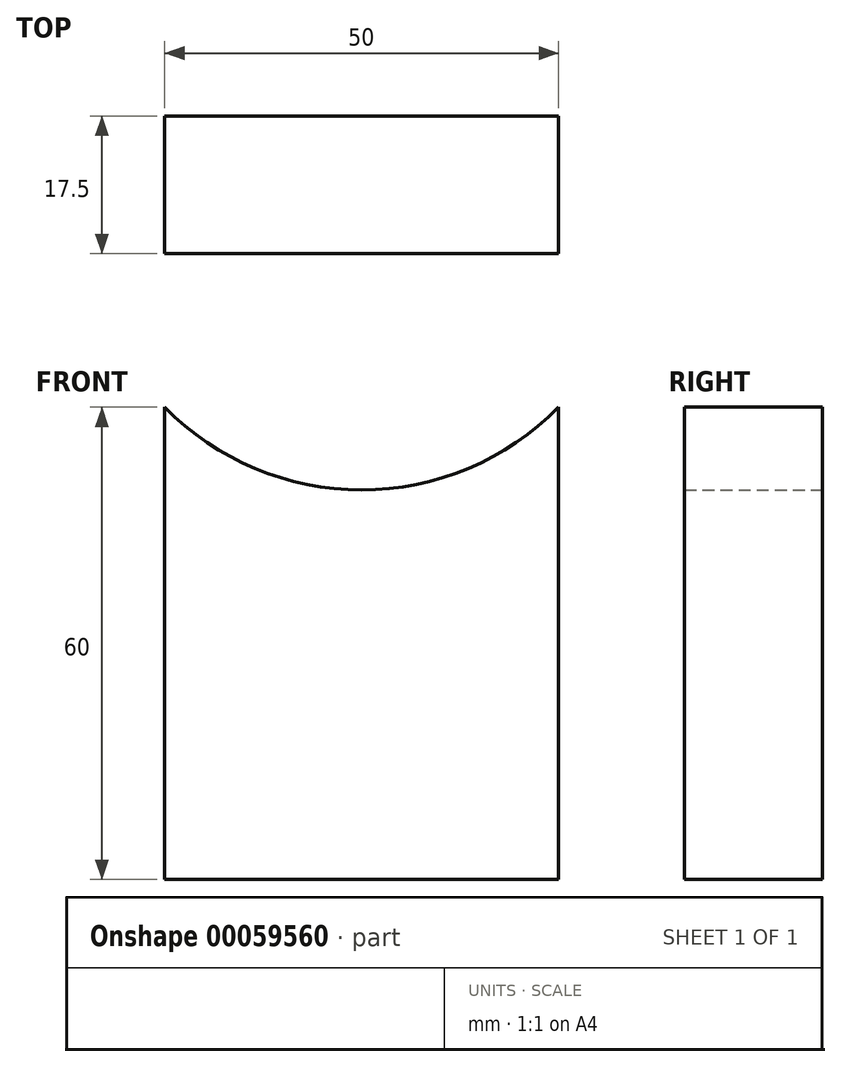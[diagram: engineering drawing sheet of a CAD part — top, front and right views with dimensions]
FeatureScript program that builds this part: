
annotation { "Feature Type Name" : "Feature", "Feature Type Description" : "" }
export const myFeature = defineFeature(function(context is Context, id is Id, definition is map)
    precondition{}
    {
        {
            var Q0;
            Q0=qCreatedBy(makeId("Front.planeOp"),FACE);
            var sketch = newSketch(context, id + "F0", { "sketchPlane" : qUnion([Q0])});
            skLineSegment(sketch, "E0.rect.top", {"start": v(-25, -30) * mm, "end": v(25, -30) * mm});
            skLineSegment(sketch, "E0.rect.left", {"start": v(-25, 30) * mm, "end": v(-25, -30) * mm});
            skLineSegment(sketch, "E0.rect.right", {"start": v(25, 30) * mm, "end": v(25, -30) * mm});
            skPoint(sketch, "E0.rect.middle", {"position": v(0, 0) * mm});
            skArc(sketch, "E1", {"start": v(-25, 30) * mm, "mid": v(0, 19.5) * mm, "end": v(25, 30) * mm});
            skSolve(sketch);
        }
        {
            var Q0;
            Q0=makeQuery(id+"F0.imprint","IMPRINT",FACE,{"disambiguationData":[TD([[makeQuery(id+"F0.imprint","IMPRINT",EDGE,{"derivedFrom":sQuery(id+"F0.wireOp",EDGE,"E0.rect.top")}),1.0]])]});
            extrude(context, id + "F1", {"entities" : qUnion([Q0]), "depth" : 17.5 * mm});
        }
    });
